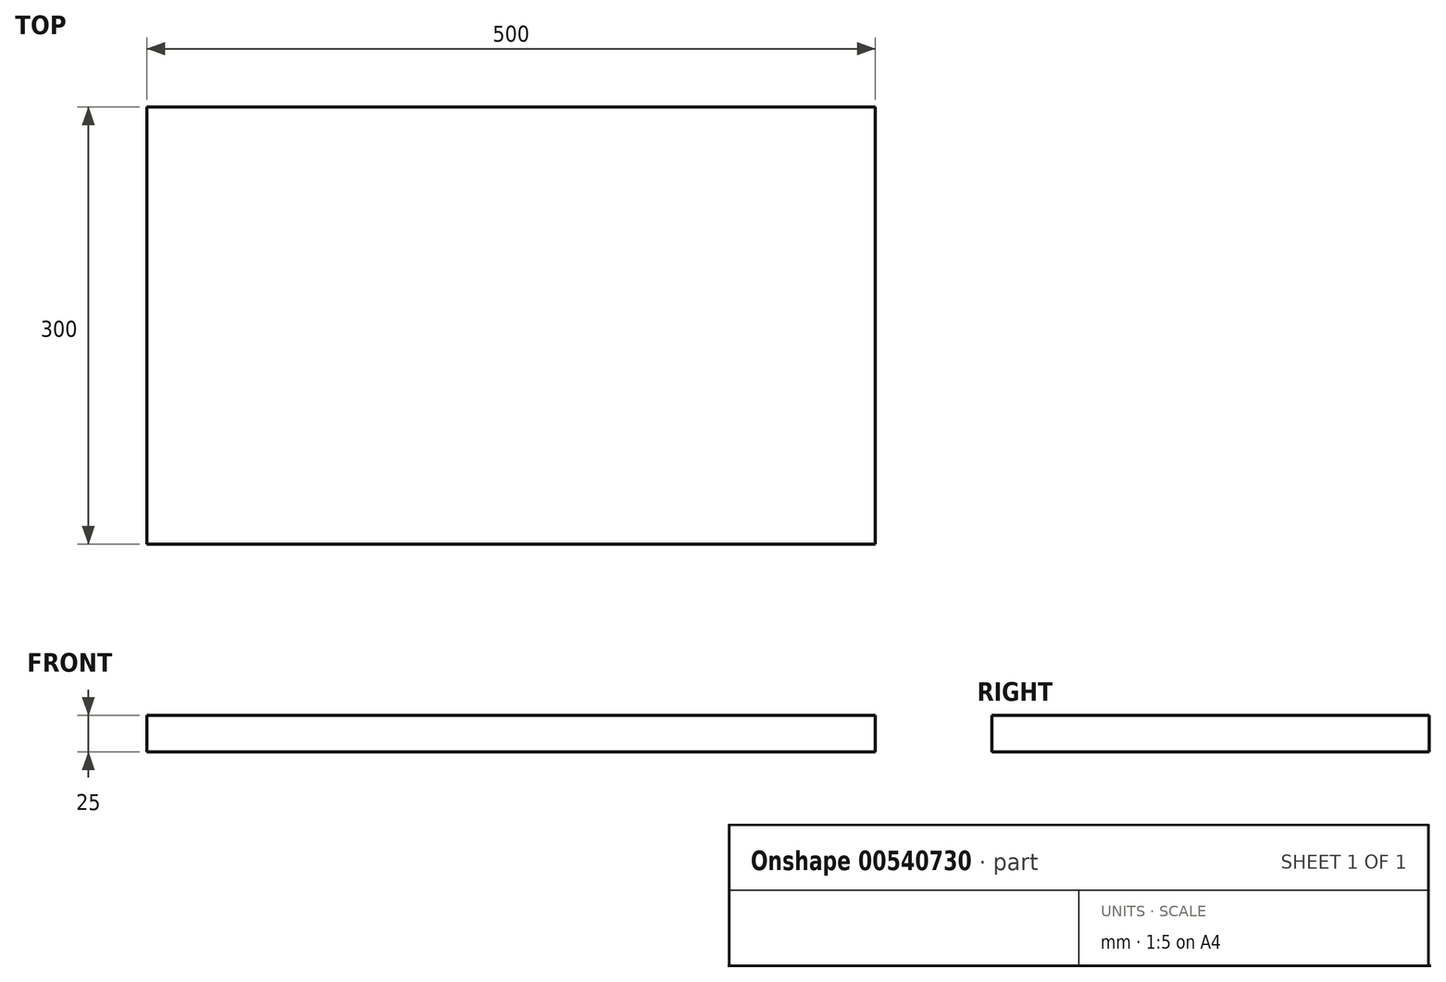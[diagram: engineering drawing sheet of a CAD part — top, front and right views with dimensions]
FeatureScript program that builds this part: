
annotation { "Feature Type Name" : "Feature", "Feature Type Description" : "" }
export const myFeature = defineFeature(function(context is Context, id is Id, definition is map)
    precondition{}
    {
        {
            var Q0;
            Q0=qCreatedBy(makeId("Top.planeOp"),FACE);
            var sketch = newSketch(context, id + "F0", { "sketchPlane" : qUnion([Q0])});
            skLineSegment(sketch, "E0.bottom", {"start": v(0, 0) * mm, "end": v(0, 0) * mm});
            skLineSegment(sketch, "E0.top", {"start": v(0, 0) * mm, "end": v(0, 0) * mm});
            skLineSegment(sketch, "E0.left", {"start": v(0, 0) * mm, "end": v(0, 0) * mm});
            skLineSegment(sketch, "E0.right", {"start": v(0, 0) * mm, "end": v(0, 0) * mm});
            skLineSegment(sketch, "E1.bottom", {"start": v(-213.56, -160.12) * mm, "end": v(286.44, -160.12) * mm});
            skLineSegment(sketch, "E1.top", {"start": v(-213.56, 139.88) * mm, "end": v(286.44, 139.88) * mm});
            skLineSegment(sketch, "E1.left", {"start": v(-213.56, -160.12) * mm, "end": v(-213.56, 139.88) * mm});
            skLineSegment(sketch, "E1.right", {"start": v(286.44, -160.12) * mm, "end": v(286.44, 139.88) * mm});
            skSolve(sketch);
        }
        {
            var Q0;
            Q0=makeQuery(id+"F0.imprint","IMPRINT",FACE,{"disambiguationData":[TD([[makeQuery(id+"F0.imprint","IMPRINT",EDGE,{"derivedFrom":sQuery(id+"F0.wireOp",EDGE,"E1.bottom")}),1.0]])]});
            extrude(context, id + "F1", {"entities" : qUnion([Q0]), "depth" : 25 * mm, "offsetDistance" : 25 * mm});
        }
    });
